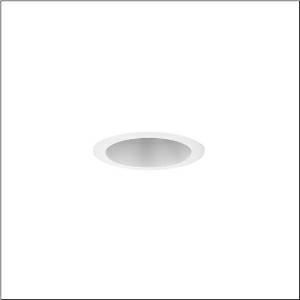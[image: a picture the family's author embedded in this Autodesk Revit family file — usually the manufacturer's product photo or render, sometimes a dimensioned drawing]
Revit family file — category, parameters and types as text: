
# Revit family: lunis_31_mini_51dn15de31
name_source: partatom
category: Lighting Fixtures
units: mm (PartAtom-declared; Revit-internal decimal feet)

## family parameters
Cut with Voids When Loaded = No
Host = Face
Light Source = No
Part Type = Normal
Room Calculation Point = No
Round Connector Dimension = Use Diameter
Shared = No

## types (1)
- Lunis 31 mini (1 x LED, 1000 lm, 8.3 W, 3000K)
    Apparent Load = 8 VA
    CIE Flux Codes = 93 98 100 100 100
    Color Rendering = 80
    Color Temperature = 3000K
    Default Elevation = 1800 mm
    Description = Lunis 31,  mini, downlight, light control with reflector, light emission: direct distribution, LED rated luminous flux: 1.000lm, light colour: 830, control gear: ECG DALI, mains connection: 220..240V, AC, 50/60Hz, housing, white, protection rating (complete): IP20, insulation class (complete): insulation class II (safety insulation), certification: CE, packaging unit: 1 piece
    Height = 0 mm  [stored 0 ft]
    Lamp = 1 x LED
    Lamp Light Flux = 1000 lm
    Lamp Power = 8.3 W
    Lamp count = 1
    Length = 188 mm  [stored 0.616798 ft]
    Luminous efficacy = 120 lm/W
    Manufacturer = Siteco
    ModVariant = No
    Model = 51DN15DE31
    Mounting Place = Ceiling
    Mounting Type = Recessed
    Number of Poles = 1
    OnlyDefault = Yes
    Power Factor = 1
    Product Name = Lunis 31 mini
    Product group = downlight | ceiling recessed
    ProductGroupID = 402
    Protection Class = Protection class II
    Protection Degree = IP 20
    RLX_Detail_Level = 1
    RlxData = <blob elided: 21781 chars, md5=68a28487>
    Socket = socket
    Standby Power = 0 W
    System Light Flux = 1000 lm
    System Power = 8 W
    Type Comments = Product without accessories
    Type Image = l_1005624.jpg
    URL = http://relux.com
    VarID = ---
    Voltage = 0 V
    Weight = 0.00 kg
    Width = 0 mm  [stored 0 ft]

note: [stored X ft] marks values corroborated as IEEE doubles in the binary element streams (Revit-internal decimal feet)

## geometry (parser evidence)
native form markers: Blend x4, Sweep x10
no freeform markers — native parametric forms only
